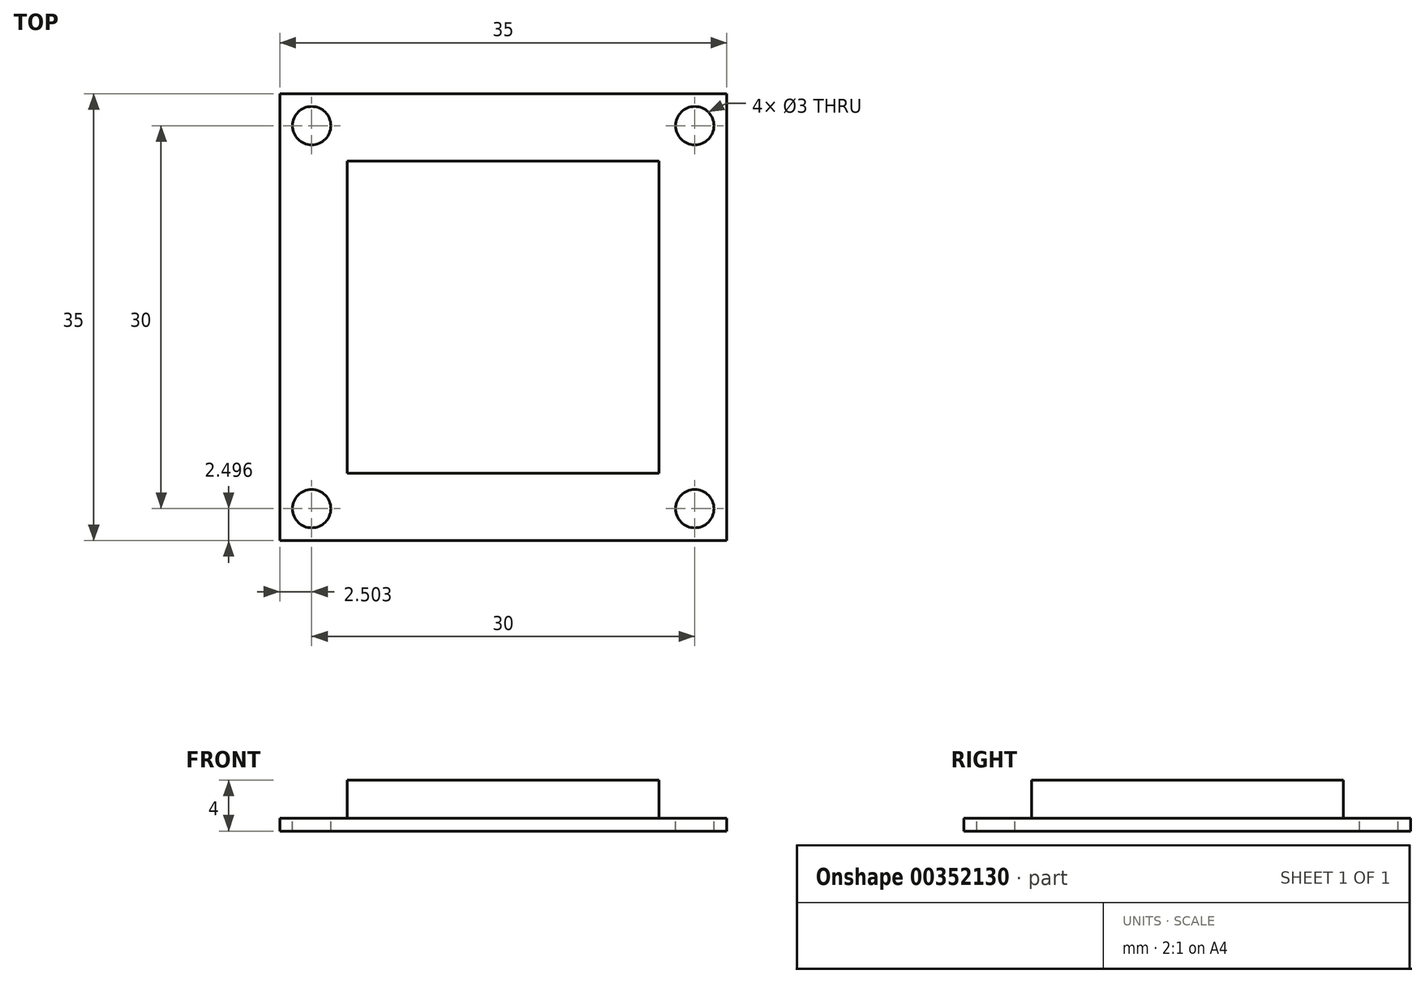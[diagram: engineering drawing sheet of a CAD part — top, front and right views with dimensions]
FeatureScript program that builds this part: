
annotation { "Feature Type Name" : "Feature", "Feature Type Description" : "" }
export const myFeature = defineFeature(function(context is Context, id is Id, definition is map)
    precondition{}
    {
        {
            var Q0;
            Q0=qCreatedBy(makeId("Top.planeOp"),FACE);
            var sketch = newSketch(context, id + "F0", { "sketchPlane" : qUnion([Q0])});
            skLineSegment(sketch, "E0.bottom", {"start": v(-17.26, 17.1) * mm, "end": v(17.74, 17.1) * mm});
            skLineSegment(sketch, "E0.top", {"start": v(-17.26, -17.9) * mm, "end": v(17.74, -17.9) * mm});
            skLineSegment(sketch, "E0.left", {"start": v(-17.26, 17.1) * mm, "end": v(-17.26, -17.9) * mm});
            skLineSegment(sketch, "E0.right", {"start": v(17.74, 17.1) * mm, "end": v(17.74, -17.9) * mm});
            skSolve(sketch);
        }
        {
            var Q0;
            Q0=makeQuery(id+"F0.imprint","IMPRINT",FACE,{"disambiguationData":[TD([[makeQuery(id+"F0.imprint","IMPRINT",EDGE,{"derivedFrom":sQuery(id+"F0.wireOp",EDGE,"E0.bottom")}),-1.0]])]});
            extrude(context, id + "F1", {"entities" : qUnion([Q0]), "depth" : 1 * mm});
        }
        {
            var Q0;
            Q0=makeQuery(id+"F1.opExtrude","CAP_FACE",FACE,{"disambiguationData":[OSD([sQuery(id+"F0.wireOp",EDGE,"E0.bottom"),sQuery(id+"F0.wireOp",EDGE,"E0.top"),sQuery(id+"F0.wireOp",EDGE,"E0.left"),sQuery(id+"F0.wireOp",EDGE,"E0.right")])],"isStart":false});
            var sketch = newSketch(context, id + "F2", { "sketchPlane" : qUnion([Q0])});
            skPoint(sketch, "E1", {"position": v(-14.76, 14.6) * mm});
            skPoint(sketch, "E2", {"position": v(15.24, -15.4) * mm});
            skPoint(sketch, "E3", {"position": v(15.24, 14.6) * mm});
            skPoint(sketch, "E4", {"position": v(-14.76, -15.4) * mm});
            skLineSegment(sketch, "E5", {"start": v(0.24, -17.9) * mm, "end": v(0.24, 17.1) * mm, "construction": true});
            skLineSegment(sketch, "E6", {"start": v(-17.26, -0.4) * mm, "end": v(17.74, -0.4) * mm, "construction": true});
            skSolve(sketch);
        }
        {
            var Q0;
            Q0=sQuery(id+"F2.wireOp",VERTEX,"E1");
            var Q1;
            Q1=sQuery(id+"F2.wireOp",VERTEX,"E4");
            var Q2;
            Q2=sQuery(id+"F2.wireOp",VERTEX,"E2");
            var Q3;
            Q3=sQuery(id+"F2.wireOp",VERTEX,"E3");
            var Q4;
            Q4=makeQuery(id+"F1.opExtrude","SWEPT_BODY",BODY,{"disambiguationData":[OSD([sQuery(id+"F0.wireOp",EDGE,"E0.bottom"),sQuery(id+"F0.wireOp",EDGE,"E0.top"),sQuery(id+"F0.wireOp",EDGE,"E0.left"),sQuery(id+"F0.wireOp",EDGE,"E0.right")])]});
            hole(context, id + "F3", {"style" : HoleStyle.SIMPLE, "endStyle" : HoleEndStyle.THROUGH, "holeDiameter" : 3 * mm, "isTappedThrough" : true, "tappedDepth" : 12 * mm, "tapClearance" : 3, "locations" : qUnion([Q0, Q1, Q2, Q3]), "scope" : qUnion([Q4])});
        }
        {
            var Q0;
            Q0=makeQuery(id+"F1.opExtrude","CAP_FACE",FACE,{"disambiguationData":[OSD([sQuery(id+"F0.wireOp",EDGE,"E0.bottom"),sQuery(id+"F0.wireOp",EDGE,"E0.top"),sQuery(id+"F0.wireOp",EDGE,"E0.left"),sQuery(id+"F0.wireOp",EDGE,"E0.right")])],"isStart":false});
            var sketch = newSketch(context, id + "F4", { "sketchPlane" : qUnion([Q0])});
            skLineSegment(sketch, "E7", {"start": v(-17.26, 17.1) * mm, "end": v(17.74, -17.9) * mm, "construction": true});
            skLineSegment(sketch, "E8", {"start": v(-17.26, -17.9) * mm, "end": v(17.74, 17.1) * mm, "construction": true});
            skLineSegment(sketch, "E9.bottom", {"start": v(-11.97, 11.8) * mm, "end": v(12.45, 11.8) * mm});
            skLineSegment(sketch, "E9.top", {"start": v(-11.97, -12.61) * mm, "end": v(12.45, -12.61) * mm});
            skLineSegment(sketch, "E9.left", {"start": v(-11.97, 11.8) * mm, "end": v(-11.97, -12.61) * mm});
            skLineSegment(sketch, "E9.right", {"start": v(12.45, 11.8) * mm, "end": v(12.45, -12.61) * mm});
            skSolve(sketch);
        }
        {
            var Q0;
            Q0 = qSketchRegion(id + "F4", true);
            extrude(context, id + "F5", {"entities" : qUnion([Q0]), "operationType" : NewBodyOperationType.ADD, "depth" : 3 * mm});
        }
    });
